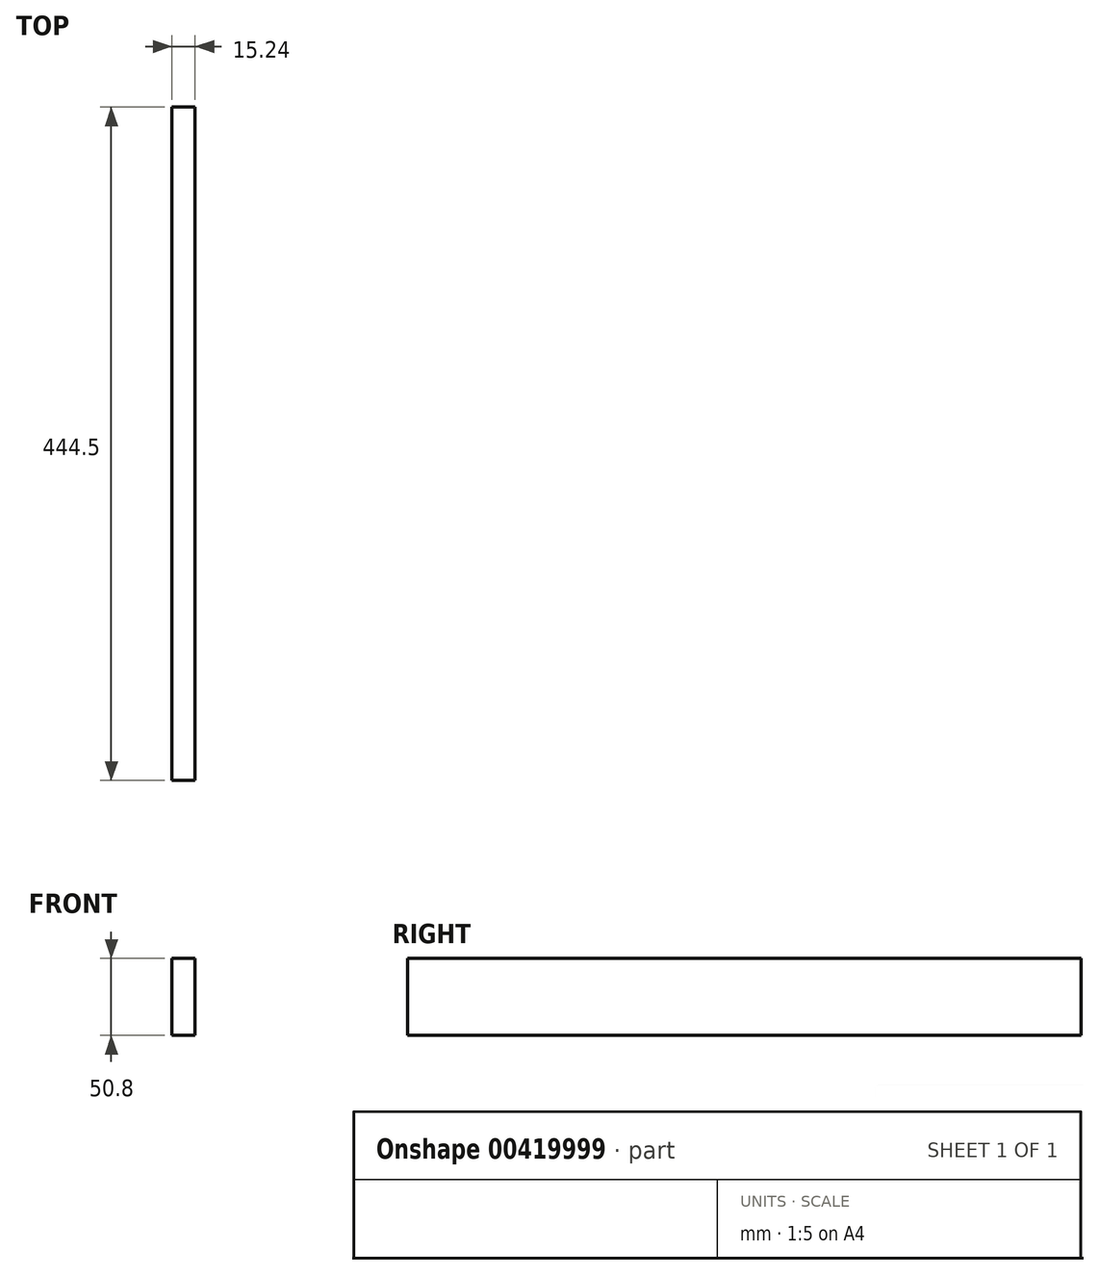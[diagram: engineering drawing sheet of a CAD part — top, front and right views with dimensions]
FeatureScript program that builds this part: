
annotation { "Feature Type Name" : "Feature", "Feature Type Description" : "" }
export const myFeature = defineFeature(function(context is Context, id is Id, definition is map)
    precondition{}
    {
        {
            var Q0;
            Q0=qCreatedBy(makeId("Front.planeOp"),FACE);
            var sketch = newSketch(context, id + "F0", { "sketchPlane" : qUnion([Q0])});
            skLineSegment(sketch, "E0.bottom", {"start": v(7.62, -25.4) * mm, "end": v(-7.62, -25.4) * mm});
            skLineSegment(sketch, "E0.top", {"start": v(7.62, 25.4) * mm, "end": v(-7.62, 25.4) * mm});
            skLineSegment(sketch, "E0.left", {"start": v(7.62, -25.4) * mm, "end": v(7.62, 25.4) * mm});
            skLineSegment(sketch, "E0.right", {"start": v(-7.62, -25.4) * mm, "end": v(-7.62, 25.4) * mm});
            skPoint(sketch, "E0.middle", {"position": v(0, 0) * mm});
            skSolve(sketch);
        }
        {
            var Q0;
            Q0=makeQuery(id+"F0.imprint","IMPRINT",FACE,{"disambiguationData":[TD([[makeQuery(id+"F0.imprint","IMPRINT",EDGE,{"derivedFrom":sQuery(id+"F0.wireOp",EDGE,"E0.bottom")}),-1.0]])]});
            extrude(context, id + "F1", {"entities" : qUnion([Q0]), "depth" : 444.5 * mm});
        }
    });
